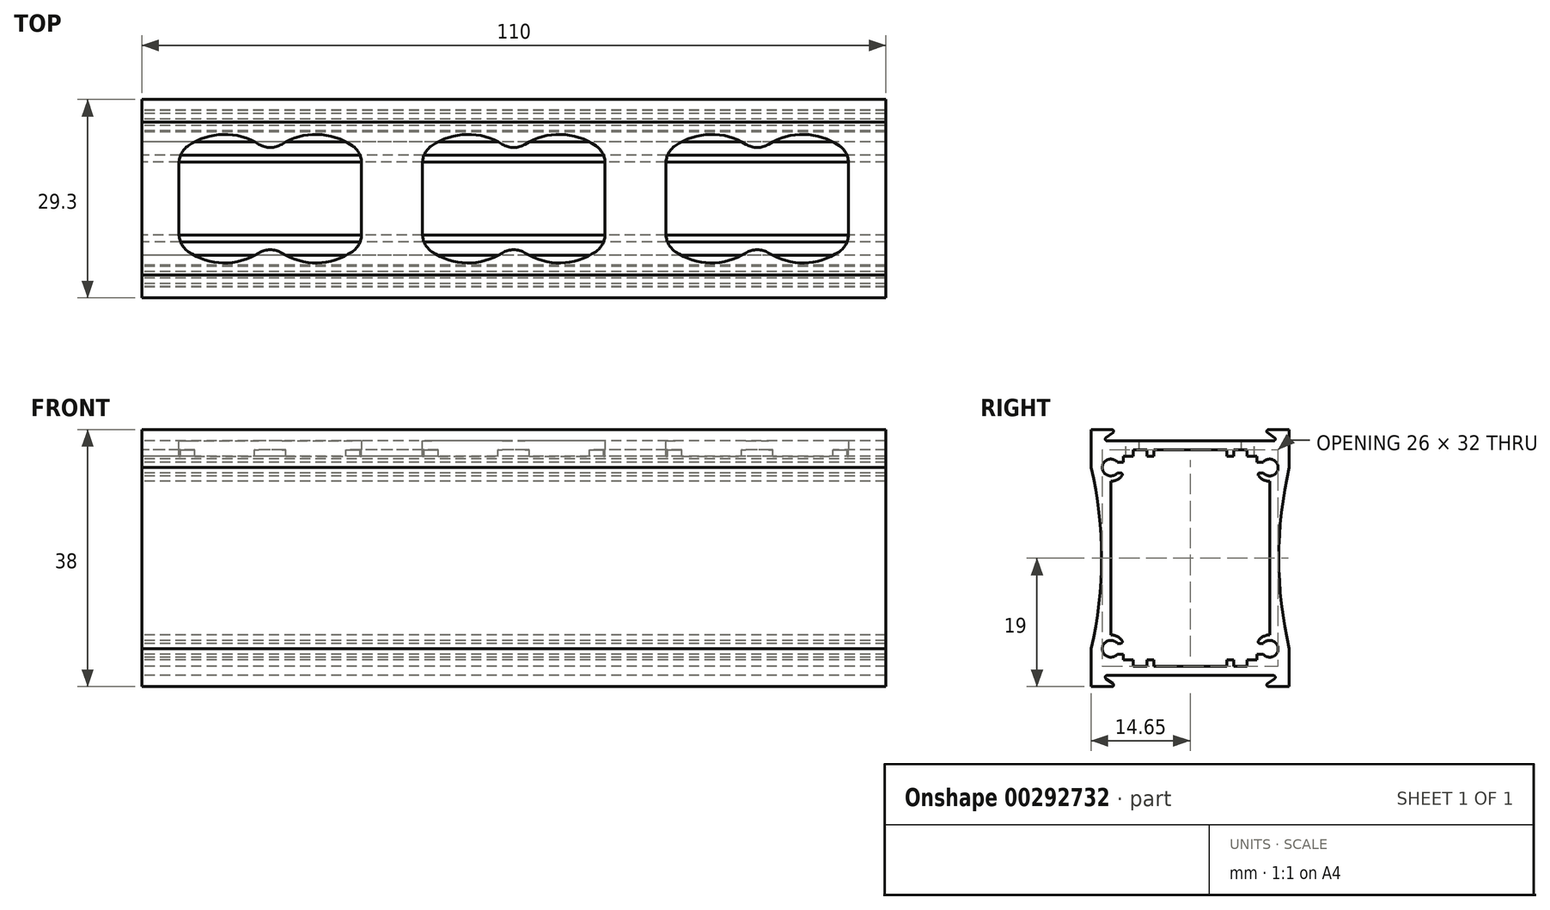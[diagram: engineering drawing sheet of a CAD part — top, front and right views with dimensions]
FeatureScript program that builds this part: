
annotation { "Feature Type Name" : "Feature", "Feature Type Description" : "" }
export const myFeature = defineFeature(function(context is Context, id is Id, definition is map)
    precondition{}
    {
        {
            var Q0;
            Q0=qCreatedBy(makeId("Right.planeOp"),FACE);
            var sketch = newSketch(context, id + "F0", { "sketchPlane" : qUnion([Q0])});
            skPoint(sketch, "E0.middle", {"position": v(0, 0) * mm});
            skLineSegment(sketch, "E1.0", {"start": v(0, 17.35) * mm, "end": v(-12.32, 17.35) * mm});
            skLineSegment(sketch, "E1.3", {"start": v(-13.1, 17.35) * mm, "end": v(-13.1, 0) * mm, "construction": true});
            skLineSegment(sketch, "E2.bottom", {"start": v(-11.57, 19) * mm, "end": v(-14.65, 19) * mm});
            skLineSegment(sketch, "E2.right", {"start": v(-14.65, 19) * mm, "end": v(-14.65, 13.4) * mm});
            skLineSegment(sketch, "E3", {"start": v(0, 0) * mm, "end": v(0, 16) * mm, "construction": true});
            skLineSegment(sketch, "E4", {"start": v(0, 0) * mm, "end": v(-11.75, 0) * mm, "construction": true});
            skArc(sketch, "E5", {"start": v(-10.79, 14.2) * mm, "mid": v(-13, 13.4) * mm, "end": v(-10.79, 12.6) * mm});
            skArc(sketch, "E6", {"start": v(-13.1, 0) * mm, "mid": v(-13.49, 6.74) * mm, "end": v(-14.65, 13.4) * mm});
            skLineSegment(sketch, "E7", {"start": v(-11.75, 13.4) * mm, "end": v(-14.65, 13.4) * mm, "construction": true});
            skArc(sketch, "E8.0", {"start": v(-11.75, 11.35) * mm, "mid": v(-10.81, 11.58) * mm, "end": v(-10.08, 12.2) * mm});
            skLineSegment(sketch, "E9.trimOffspring", {"start": v(-11.75, 11.35) * mm, "end": v(-11.75, 0) * mm});
            skLineSegment(sketch, "E10", {"start": v(-11.75, 13.4) * mm, "end": v(-9.7, 13.4) * mm, "construction": true});
            skLineSegment(sketch, "E11.0", {"start": v(-10.79, 12.6) * mm, "end": v(-10.29, 12.6) * mm});
            skLineSegment(sketch, "E12", {"start": v(-11.75, 16) * mm, "end": v(-11.75, 11.35) * mm, "construction": true});
            skLineSegment(sketch, "E13.trimOffspring", {"start": v(-10.79, 14.2) * mm, "end": v(-9.86, 14.2) * mm});
            skLineSegment(sketch, "E14", {"start": v(-10.79, 14.2) * mm, "end": v(-10.79, 12.6) * mm, "construction": true});
            skLineSegment(sketch, "E15", {"start": v(-9.86, 14.2) * mm, "end": v(-9.86, 15.05) * mm});
            skLineSegment(sketch, "E16", {"start": v(-9.86, 15.05) * mm, "end": v(-8.4, 15.05) * mm});
            skLineSegment(sketch, "E17", {"start": v(-8.4, 15.05) * mm, "end": v(-8.4, 16) * mm});
            skLineSegment(sketch, "E18", {"start": v(-8.4, 16) * mm, "end": v(-6.4, 16) * mm});
            skLineSegment(sketch, "E19", {"start": v(-6.4, 16) * mm, "end": v(-6.4, 15.05) * mm});
            skLineSegment(sketch, "E20", {"start": v(-6.4, 15.05) * mm, "end": v(-5.4, 15.05) * mm});
            skLineSegment(sketch, "E21", {"start": v(-5.4, 15.05) * mm, "end": v(-5.4, 16) * mm});
            skLineSegment(sketch, "E22", {"start": v(-5.4, 16) * mm, "end": v(0, 16) * mm});
            skLineSegment(sketch, "E23", {"start": v(-10.79, 14.2) * mm, "end": v(-10.79, 19) * mm, "construction": true});
            skLineSegment(sketch, "E24", {"start": v(-12.47, 17.8) * mm, "end": v(-11.42, 18.55) * mm});
            skPoint(sketch, "E25.visualSharp", {"position": v(-10.79, 19) * mm});
            skArc(sketch, "E25.filletArc", {"start": v(-11.42, 18.55) * mm, "mid": v(-11.33, 18.83) * mm, "end": v(-11.57, 19) * mm});
            skPoint(sketch, "E26.visualSharp", {"position": v(-13.1, 17.35) * mm});
            skArc(sketch, "E26.filletArc", {"start": v(-12.47, 17.8) * mm, "mid": v(-12.56, 17.52) * mm, "end": v(-12.32, 17.35) * mm});
            skPoint(sketch, "E27.visualSharp", {"position": v(-9.86, 12.6) * mm});
            skArc(sketch, "E27.filletArc", {"start": v(-10.08, 12.2) * mm, "mid": v(-10.07, 12.46) * mm, "end": v(-10.29, 12.6) * mm});
            skArc(sketch, "E28.MirrorCS", {"start": v(10.08, 12.2) * mm, "mid": v(10.07, 12.46) * mm, "end": v(10.29, 12.6) * mm});
            skLineSegment(sketch, "E29.MirrorCS", {"start": v(10.79, 12.6) * mm, "end": v(10.29, 12.6) * mm});
            skLineSegment(sketch, "E30.MirrorCS", {"start": v(11.75, 13.4) * mm, "end": v(9.7, 13.4) * mm, "construction": true});
            skLineSegment(sketch, "E31.MirrorCS", {"start": v(10.79, 14.2) * mm, "end": v(10.79, 12.6) * mm, "construction": true});
            skLineSegment(sketch, "E32.MirrorCS", {"start": v(9.86, 15.05) * mm, "end": v(8.4, 15.05) * mm});
            skLineSegment(sketch, "E33.MirrorCS", {"start": v(12.47, 17.8) * mm, "end": v(11.42, 18.55) * mm});
            skLineSegment(sketch, "E34.MirrorCS", {"start": v(10.79, 14.2) * mm, "end": v(9.86, 14.2) * mm});
            skLineSegment(sketch, "E35.MirrorCS", {"start": v(9.86, 14.2) * mm, "end": v(9.86, 15.05) * mm});
            skArc(sketch, "E36.MirrorCS", {"start": v(11.75, 11.35) * mm, "mid": v(10.81, 11.58) * mm, "end": v(10.08, 12.2) * mm});
            skArc(sketch, "E37.MirrorCS", {"start": v(12.47, 17.8) * mm, "mid": v(12.56, 17.52) * mm, "end": v(12.32, 17.35) * mm});
            skArc(sketch, "E38.MirrorCS", {"start": v(11.42, 18.55) * mm, "mid": v(11.33, 18.83) * mm, "end": v(11.57, 19) * mm});
            skLineSegment(sketch, "E39.MirrorCS", {"start": v(5.4, 15.05) * mm, "end": v(5.4, 16) * mm});
            skLineSegment(sketch, "E40.MirrorCS", {"start": v(6.4, 15.05) * mm, "end": v(5.4, 15.05) * mm});
            skLineSegment(sketch, "E41.MirrorCS", {"start": v(8.4, 15.05) * mm, "end": v(8.4, 16) * mm});
            skLineSegment(sketch, "E42.MirrorCS", {"start": v(8.4, 16) * mm, "end": v(6.4, 16) * mm});
            skLineSegment(sketch, "E43.MirrorCS", {"start": v(6.4, 16) * mm, "end": v(6.4, 15.05) * mm});
            skLineSegment(sketch, "E44.MirrorCS", {"start": v(11.75, 13.4) * mm, "end": v(14.65, 13.4) * mm, "construction": true});
            skLineSegment(sketch, "E45.MirrorCS", {"start": v(10.79, 14.2) * mm, "end": v(10.79, 19) * mm, "construction": true});
            skPoint(sketch, "E46.MirrorP", {"position": v(9.86, 12.6) * mm});
            skLineSegment(sketch, "E47.MirrorCS", {"start": v(11.75, 16) * mm, "end": v(11.75, 11.35) * mm, "construction": true});
            skLineSegment(sketch, "E48.MirrorCS", {"start": v(11.57, 19) * mm, "end": v(14.65, 19) * mm});
            skArc(sketch, "E49.MirrorCS", {"start": v(10.79, 14.2) * mm, "mid": v(13, 13.4) * mm, "end": v(10.79, 12.6) * mm});
            skLineSegment(sketch, "E50.MirrorCS", {"start": v(11.75, 11.35) * mm, "end": v(11.75, 0) * mm});
            skPoint(sketch, "E51.MirrorP", {"position": v(10.79, 19) * mm});
            skPoint(sketch, "E52.MirrorP", {"position": v(13.1, 17.35) * mm});
            skLineSegment(sketch, "E53.MirrorCS", {"start": v(0, 0) * mm, "end": v(11.75, 0) * mm, "construction": true});
            skArc(sketch, "E54.MirrorCS", {"start": v(13.1, 0) * mm, "mid": v(13.49, 6.74) * mm, "end": v(14.65, 13.4) * mm});
            skLineSegment(sketch, "E55.MirrorCS", {"start": v(5.4, 16) * mm, "end": v(0, 16) * mm});
            skLineSegment(sketch, "E56.MirrorCS", {"start": v(0, 17.35) * mm, "end": v(12.32, 17.35) * mm});
            skLineSegment(sketch, "E57.MirrorCS", {"start": v(13.1, 17.35) * mm, "end": v(13.1, 0) * mm, "construction": true});
            skLineSegment(sketch, "E58.MirrorCS", {"start": v(14.65, 19) * mm, "end": v(14.65, 13.4) * mm});
            skLineSegment(sketch, "E59.MirrorCS", {"start": v(-10.79, -12.6) * mm, "end": v(-10.29, -12.6) * mm});
            skArc(sketch, "E60.MirrorCS", {"start": v(-10.08, -12.2) * mm, "mid": v(-10.07, -12.46) * mm, "end": v(-10.29, -12.6) * mm});
            skLineSegment(sketch, "E61.MirrorCS", {"start": v(-11.75, -13.4) * mm, "end": v(-9.7, -13.4) * mm, "construction": true});
            skLineSegment(sketch, "E62.MirrorCS", {"start": v(11.75, -13.4) * mm, "end": v(9.7, -13.4) * mm, "construction": true});
            skLineSegment(sketch, "E63.MirrorCS", {"start": v(10.79, -12.6) * mm, "end": v(10.29, -12.6) * mm});
            skArc(sketch, "E64.MirrorCS", {"start": v(10.08, -12.2) * mm, "mid": v(10.07, -12.46) * mm, "end": v(10.29, -12.6) * mm});
            skLineSegment(sketch, "E65.MirrorCS", {"start": v(-10.79, -14.2) * mm, "end": v(-10.79, -12.6) * mm, "construction": true});
            skLineSegment(sketch, "E66.MirrorCS", {"start": v(-12.47, -17.8) * mm, "end": v(-11.42, -18.55) * mm});
            skLineSegment(sketch, "E67.MirrorCS", {"start": v(12.47, -17.8) * mm, "end": v(11.42, -18.55) * mm});
            skLineSegment(sketch, "E68.MirrorCS", {"start": v(-10.79, -14.2) * mm, "end": v(-9.86, -14.2) * mm});
            skArc(sketch, "E69.MirrorCS", {"start": v(12.47, -17.8) * mm, "mid": v(12.56, -17.52) * mm, "end": v(12.32, -17.35) * mm});
            skArc(sketch, "E70.MirrorCS", {"start": v(-12.47, -17.8) * mm, "mid": v(-12.56, -17.52) * mm, "end": v(-12.32, -17.35) * mm});
            skLineSegment(sketch, "E71.MirrorCS", {"start": v(10.79, -14.2) * mm, "end": v(10.79, -12.6) * mm, "construction": true});
            skArc(sketch, "E72.MirrorCS", {"start": v(11.42, -18.55) * mm, "mid": v(11.33, -18.83) * mm, "end": v(11.57, -19) * mm});
            skArc(sketch, "E73.MirrorCS", {"start": v(-11.42, -18.55) * mm, "mid": v(-11.33, -18.83) * mm, "end": v(-11.57, -19) * mm});
            skLineSegment(sketch, "E74.MirrorCS", {"start": v(9.86, -14.2) * mm, "end": v(9.86, -15.05) * mm});
            skArc(sketch, "E75.MirrorCS", {"start": v(-11.75, -11.35) * mm, "mid": v(-10.81, -11.58) * mm, "end": v(-10.08, -12.2) * mm});
            skLineSegment(sketch, "E76.MirrorCS", {"start": v(10.79, -14.2) * mm, "end": v(9.86, -14.2) * mm});
            skLineSegment(sketch, "E77.MirrorCS", {"start": v(-9.86, -14.2) * mm, "end": v(-9.86, -15.05) * mm});
            skLineSegment(sketch, "E78.MirrorCS", {"start": v(-8.4, -15.05) * mm, "end": v(-8.4, -16) * mm});
            skLineSegment(sketch, "E79.MirrorCS", {"start": v(-5.4, -15.05) * mm, "end": v(-5.4, -16) * mm});
            skLineSegment(sketch, "E80.MirrorCS", {"start": v(-6.4, -16) * mm, "end": v(-6.4, -15.05) * mm});
            skLineSegment(sketch, "E81.MirrorCS", {"start": v(-6.4, -15.05) * mm, "end": v(-5.4, -15.05) * mm});
            skLineSegment(sketch, "E82.MirrorCS", {"start": v(-9.86, -15.05) * mm, "end": v(-8.4, -15.05) * mm});
            skArc(sketch, "E83.MirrorCS", {"start": v(11.75, -11.35) * mm, "mid": v(10.81, -11.58) * mm, "end": v(10.08, -12.2) * mm});
            skLineSegment(sketch, "E84.MirrorCS", {"start": v(5.4, -15.05) * mm, "end": v(5.4, -16) * mm});
            skLineSegment(sketch, "E85.MirrorCS", {"start": v(-8.4, -16) * mm, "end": v(-6.4, -16) * mm});
            skLineSegment(sketch, "E86.MirrorCS", {"start": v(8.4, -15.05) * mm, "end": v(8.4, -16) * mm});
            skLineSegment(sketch, "E87.MirrorCS", {"start": v(6.4, -15.05) * mm, "end": v(5.4, -15.05) * mm});
            skLineSegment(sketch, "E88.MirrorCS", {"start": v(6.4, -16) * mm, "end": v(6.4, -15.05) * mm});
            skLineSegment(sketch, "E89.MirrorCS", {"start": v(8.4, -16) * mm, "end": v(6.4, -16) * mm});
            skLineSegment(sketch, "E90.MirrorCS", {"start": v(9.86, -15.05) * mm, "end": v(8.4, -15.05) * mm});
            skLineSegment(sketch, "E91.MirrorCS", {"start": v(11.75, -16) * mm, "end": v(11.75, -11.35) * mm, "construction": true});
            skPoint(sketch, "E92.MirrorP", {"position": v(-9.86, -12.6) * mm});
            skLineSegment(sketch, "E93.MirrorCS", {"start": v(-10.79, -14.2) * mm, "end": v(-10.79, -19) * mm, "construction": true});
            skLineSegment(sketch, "E94.MirrorCS", {"start": v(-11.75, -16) * mm, "end": v(-11.75, -11.35) * mm, "construction": true});
            skLineSegment(sketch, "E95.MirrorCS", {"start": v(-11.57, -19) * mm, "end": v(-14.65, -19) * mm});
            skLineSegment(sketch, "E96.MirrorCS", {"start": v(-11.75, -13.4) * mm, "end": v(-14.65, -13.4) * mm, "construction": true});
            skPoint(sketch, "E97.MirrorP", {"position": v(-10.79, -19) * mm});
            skLineSegment(sketch, "E98.MirrorCS", {"start": v(14.65, -19) * mm, "end": v(14.65, -13.4) * mm});
            skLineSegment(sketch, "E99.MirrorCS", {"start": v(-13.1, -17.35) * mm, "end": v(-13.1, 0) * mm, "construction": true});
            skPoint(sketch, "E100.MirrorP", {"position": v(-13.1, -17.35) * mm});
            skLineSegment(sketch, "E101.MirrorCS", {"start": v(-11.75, -11.35) * mm, "end": v(-11.75, 0) * mm});
            skPoint(sketch, "E102.MirrorP", {"position": v(10.79, -19) * mm});
            skLineSegment(sketch, "E103.MirrorCS", {"start": v(5.4, -16) * mm, "end": v(0, -16) * mm});
            skLineSegment(sketch, "E104.MirrorCS", {"start": v(11.75, -11.35) * mm, "end": v(11.75, 0) * mm});
            skLineSegment(sketch, "E105.MirrorCS", {"start": v(10.79, -14.2) * mm, "end": v(10.79, -19) * mm, "construction": true});
            skPoint(sketch, "E106.MirrorP", {"position": v(9.86, -12.6) * mm});
            skLineSegment(sketch, "E107.MirrorCS", {"start": v(0, -17.35) * mm, "end": v(12.32, -17.35) * mm});
            skLineSegment(sketch, "E108.MirrorCS", {"start": v(-5.4, -16) * mm, "end": v(0, -16) * mm});
            skLineSegment(sketch, "E109.MirrorCS", {"start": v(13.1, -17.35) * mm, "end": v(13.1, 0) * mm, "construction": true});
            skArc(sketch, "E110.MirrorCS", {"start": v(10.79, -14.2) * mm, "mid": v(13, -13.4) * mm, "end": v(10.79, -12.6) * mm});
            skPoint(sketch, "E111.MirrorP", {"position": v(13.1, -17.35) * mm});
            skArc(sketch, "E112.MirrorCS", {"start": v(-10.79, -14.2) * mm, "mid": v(-13, -13.4) * mm, "end": v(-10.79, -12.6) * mm});
            skLineSegment(sketch, "E113.MirrorCS", {"start": v(11.57, -19) * mm, "end": v(14.65, -19) * mm});
            skLineSegment(sketch, "E114.MirrorCS", {"start": v(0, 0) * mm, "end": v(0, -16) * mm, "construction": true});
            skLineSegment(sketch, "E115.MirrorCS", {"start": v(-14.65, -19) * mm, "end": v(-14.65, -13.4) * mm});
            skLineSegment(sketch, "E116.MirrorCS", {"start": v(0, -17.35) * mm, "end": v(-12.32, -17.35) * mm});
            skLineSegment(sketch, "E117.MirrorCS", {"start": v(11.75, -13.4) * mm, "end": v(14.65, -13.4) * mm, "construction": true});
            skArc(sketch, "E118.MirrorCS", {"start": v(-13.1, 0) * mm, "mid": v(-13.49, -6.74) * mm, "end": v(-14.65, -13.4) * mm});
            skArc(sketch, "E119.MirrorCS", {"start": v(13.1, 0) * mm, "mid": v(13.49, -6.74) * mm, "end": v(14.65, -13.4) * mm});
            skSolve(sketch);
        }
        {
            var Q0;
            Q0=makeQuery(id+"F0.imprint","IMPRINT",FACE,{"disambiguationData":[TD([[makeQuery(id+"F0.imprint","IMPRINT",EDGE,{"derivedFrom":sQuery(id+"F0.wireOp",EDGE,"E1.0")}),1.0]])]});
            extrude(context, id + "F1", {"entities" : qUnion([Q0]), "depth" : 110 * mm});
        }
        {
            var Q0;
            Q0=makeQuery(id+"F1.opExtrude","SWEPT_FACE",FACE,{"disambiguationData":[OSD([sQuery(id+"F0.wireOp",EDGE,"E48.MirrorCS")])]});
            var sketch = newSketch(context, id + "F2", { "sketchPlane" : qUnion([Q0])});
            skLineSegment(sketch, "E120", {"start": v(0, 0) * mm, "end": v(110, 0) * mm, "construction": true});
            skLineSegment(sketch, "E121.left", {"start": v(19, -6.68) * mm, "end": v(19, 6.68) * mm});
            skLineSegment(sketch, "E121.right", {"start": v(5.5, -6.68) * mm, "end": v(5.5, 6.68) * mm});
            skPoint(sketch, "E121.middle", {"position": v(12.25, 0) * mm});
            skArc(sketch, "E122", {"start": v(19, 6.68) * mm, "mid": v(12.25, 9.5) * mm, "end": v(5.5, 6.68) * mm});
            skArc(sketch, "E123.trimOffspring", {"start": v(5.5, -6.68) * mm, "mid": v(12.25, -9.5) * mm, "end": v(19, -6.68) * mm});
            skArc(sketch, "E124.1.0.0", {"start": v(32.5, 6.68) * mm, "mid": v(25.75, 9.5) * mm, "end": v(19, 6.68) * mm});
            skLineSegment(sketch, "E124.1.0.1", {"start": v(32.5, -6.68) * mm, "end": v(32.5, 6.68) * mm});
            skArc(sketch, "E124.1.0.2", {"start": v(19, -6.68) * mm, "mid": v(25.75, -9.5) * mm, "end": v(32.5, -6.68) * mm});
            skLineSegment(sketch, "E124.direction1", {"start": v(12.25, 0) * mm, "end": v(25.75, 0) * mm, "construction": true});
            skArc(sketch, "E125.1.0.0", {"start": v(55, 6.68) * mm, "mid": v(48.25, 9.5) * mm, "end": v(41.5, 6.68) * mm});
            skLineSegment(sketch, "E125.1.0.1", {"start": v(55, -6.68) * mm, "end": v(55, 6.68) * mm});
            skArc(sketch, "E125.1.0.2", {"start": v(68.5, 6.68) * mm, "mid": v(61.75, 9.5) * mm, "end": v(55, 6.68) * mm});
            skLineSegment(sketch, "E125.1.0.3", {"start": v(55, -6.68) * mm, "end": v(55, 6.68) * mm});
            skLineSegment(sketch, "E125.1.0.4", {"start": v(68.5, -6.68) * mm, "end": v(68.5, 6.68) * mm});
            skArc(sketch, "E125.1.0.5", {"start": v(55, -6.68) * mm, "mid": v(61.75, -9.5) * mm, "end": v(68.5, -6.68) * mm});
            skArc(sketch, "E125.1.0.6", {"start": v(41.5, -6.68) * mm, "mid": v(48.25, -9.5) * mm, "end": v(55, -6.68) * mm});
            skLineSegment(sketch, "E125.1.0.7", {"start": v(41.5, -6.68) * mm, "end": v(41.5, 6.68) * mm});
            skArc(sketch, "E125.2.0.0", {"start": v(91, 6.68) * mm, "mid": v(84.25, 9.5) * mm, "end": v(77.5, 6.68) * mm});
            skLineSegment(sketch, "E125.2.0.1", {"start": v(91, -6.68) * mm, "end": v(91, 6.68) * mm});
            skArc(sketch, "E125.2.0.2", {"start": v(104.5, 6.68) * mm, "mid": v(97.75, 9.5) * mm, "end": v(91, 6.68) * mm});
            skLineSegment(sketch, "E125.2.0.3", {"start": v(91, -6.68) * mm, "end": v(91, 6.68) * mm});
            skLineSegment(sketch, "E125.2.0.4", {"start": v(104.5, -6.68) * mm, "end": v(104.5, 6.68) * mm});
            skArc(sketch, "E125.2.0.5", {"start": v(91, -6.68) * mm, "mid": v(97.75, -9.5) * mm, "end": v(104.5, -6.68) * mm});
            skArc(sketch, "E125.2.0.6", {"start": v(77.5, -6.68) * mm, "mid": v(84.25, -9.5) * mm, "end": v(91, -6.68) * mm});
            skLineSegment(sketch, "E125.2.0.7", {"start": v(77.5, -6.68) * mm, "end": v(77.5, 6.68) * mm});
            skLineSegment(sketch, "E125.direction1", {"start": v(12.25, 0) * mm, "end": v(48.25, 0) * mm, "construction": true});
            skPoint(sketch, "E126", {"position": v(77.5, 0) * mm});
            skLineSegment(sketch, "E127", {"start": v(55, 6.68) * mm, "end": v(55, -6.68) * mm, "construction": true});
            skPoint(sketch, "E128", {"position": v(55, 0) * mm});
            skLineSegment(sketch, "E129", {"start": v(37, 4) * mm, "end": v(37, -4) * mm, "construction": true});
            skLineSegment(sketch, "E130", {"start": v(73, 4) * mm, "end": v(73, -4) * mm, "construction": true});
            skLineSegment(sketch, "E131", {"start": v(37, 4) * mm, "end": v(73, -4) * mm, "construction": true});
            skCircle(sketch, "E132", {"center": v(37, 4) * mm, "radius": 1.5 * mm, "construction": true});
            skCircle(sketch, "E133", {"center": v(37, -4) * mm, "radius": 1.5 * mm, "construction": true});
            skCircle(sketch, "E134", {"center": v(73, -4) * mm, "radius": 1.5 * mm, "construction": true});
            skCircle(sketch, "E135", {"center": v(73, 4) * mm, "radius": 1.5 * mm, "construction": true});
            skSolve(sketch);
        }
        {
            var Q0;
            Q0 = qSketchRegion(id + "F2", true);
            extrude(context, id + "F3", {"entities" : qUnion([Q0]), "operationType" : NewBodyOperationType.REMOVE, "oppositeDirection" : true, "depth" : 8 * mm});
        }
        {
            var Q0;
            Q0=makeQuery(id+"F3.boolean.opBoolean","COPY",EDGE,{"derivedFrom":makeQuery(id+"F3.opExtrude","SWEPT_EDGE",EDGE,{"disambiguationData":[OSD([sQuery(id+"F2.wireOp",EDGE,"E124.1.0.1"),sQuery(id+"F2.wireOp",EDGE,"E124.1.0.2")])]})});
            var Q1;
            Q1=makeQuery(id+"F3.boolean.opBoolean","COPY",EDGE,{"derivedFrom":makeQuery(id+"F3.opExtrude","SWEPT_EDGE",EDGE,{"disambiguationData":[OSD([sQuery(id+"F2.wireOp",EDGE,"E124.1.0.0"),sQuery(id+"F2.wireOp",EDGE,"E124.1.0.1")])]})});
            var Q2;
            Q2=makeQuery(id+"F3.boolean.opBoolean","COPY",EDGE,{"derivedFrom":makeQuery(id+"F3.opExtrude","SWEPT_EDGE",EDGE,{"disambiguationData":[OSD([sQuery(id+"F2.wireOp",EDGE,"E121.left"),sQuery(id+"F2.wireOp",EDGE,"E122")])]})});
            var Q3;
            Q3=makeQuery(id+"F3.boolean.opBoolean","COPY",EDGE,{"derivedFrom":makeQuery(id+"F3.opExtrude","SWEPT_EDGE",EDGE,{"disambiguationData":[OSD([sQuery(id+"F2.wireOp",EDGE,"E121.left"),sQuery(id+"F2.wireOp",EDGE,"E123.trimOffspring")])]})});
            var Q4;
            Q4=makeQuery(id+"F3.boolean.opBoolean","COPY",EDGE,{"derivedFrom":makeQuery(id+"F3.opExtrude","SWEPT_EDGE",EDGE,{"disambiguationData":[OSD([sQuery(id+"F2.wireOp",EDGE,"E125.1.0.1"),sQuery(id+"F2.wireOp",EDGE,"E125.1.0.6")])]})});
            var Q5;
            Q5=makeQuery(id+"F3.boolean.opBoolean","COPY",EDGE,{"derivedFrom":makeQuery(id+"F3.opExtrude","SWEPT_EDGE",EDGE,{"disambiguationData":[OSD([sQuery(id+"F2.wireOp",EDGE,"E125.1.0.0"),sQuery(id+"F2.wireOp",EDGE,"E125.1.0.1")])]})});
            var Q6;
            Q6=makeQuery(id+"F3.boolean.opBoolean","COPY",EDGE,{"derivedFrom":makeQuery(id+"F3.opExtrude","SWEPT_EDGE",EDGE,{"disambiguationData":[OSD([sQuery(id+"F2.wireOp",EDGE,"E125.1.0.2"),sQuery(id+"F2.wireOp",EDGE,"E125.1.0.4")])]})});
            var Q7;
            Q7=makeQuery(id+"F3.boolean.opBoolean","COPY",EDGE,{"derivedFrom":makeQuery(id+"F3.opExtrude","SWEPT_EDGE",EDGE,{"disambiguationData":[OSD([sQuery(id+"F2.wireOp",EDGE,"E125.1.0.4"),sQuery(id+"F2.wireOp",EDGE,"E125.1.0.5")])]})});
            var Q8;
            Q8=makeQuery(id+"F3.boolean.opBoolean","COPY",EDGE,{"derivedFrom":makeQuery(id+"F3.opExtrude","SWEPT_EDGE",EDGE,{"disambiguationData":[OSD([sQuery(id+"F2.wireOp",EDGE,"E125.2.0.1"),sQuery(id+"F2.wireOp",EDGE,"E125.2.0.6")])]})});
            var Q9;
            Q9=makeQuery(id+"F3.boolean.opBoolean","COPY",EDGE,{"derivedFrom":makeQuery(id+"F3.opExtrude","SWEPT_EDGE",EDGE,{"disambiguationData":[OSD([sQuery(id+"F2.wireOp",EDGE,"E125.2.0.0"),sQuery(id+"F2.wireOp",EDGE,"E125.2.0.1")])]})});
            var Q10;
            Q10=makeQuery(id+"F3.boolean.opBoolean","COPY",EDGE,{"derivedFrom":makeQuery(id+"F3.opExtrude","SWEPT_EDGE",EDGE,{"disambiguationData":[OSD([sQuery(id+"F2.wireOp",EDGE,"E125.2.0.2"),sQuery(id+"F2.wireOp",EDGE,"E125.2.0.4")])]})});
            var Q11;
            Q11=makeQuery(id+"F3.boolean.opBoolean","COPY",EDGE,{"derivedFrom":makeQuery(id+"F3.opExtrude","SWEPT_EDGE",EDGE,{"disambiguationData":[OSD([sQuery(id+"F2.wireOp",EDGE,"E125.2.0.4"),sQuery(id+"F2.wireOp",EDGE,"E125.2.0.5")])]})});
            var Q12;
            Q12=makeQuery(id+"F3.boolean.opBoolean","COPY",EDGE,{"derivedFrom":makeQuery(id+"F3.opExtrude","SWEPT_EDGE",EDGE,{"disambiguationData":[OSD([sQuery(id+"F2.wireOp",EDGE,"E125.2.0.2"),sQuery(id+"F2.wireOp",EDGE,"E125.2.0.3")])]})});
            var Q13;
            Q13=makeQuery(id+"F3.boolean.opBoolean","COPY",EDGE,{"derivedFrom":makeQuery(id+"F3.opExtrude","SWEPT_EDGE",EDGE,{"disambiguationData":[OSD([sQuery(id+"F2.wireOp",EDGE,"E125.2.0.3"),sQuery(id+"F2.wireOp",EDGE,"E125.2.0.5")])]})});
            var Q14;
            Q14=makeQuery(id+"F3.boolean.opBoolean","COPY",EDGE,{"derivedFrom":makeQuery(id+"F3.opExtrude","SWEPT_EDGE",EDGE,{"disambiguationData":[OSD([sQuery(id+"F2.wireOp",EDGE,"E125.2.0.6"),sQuery(id+"F2.wireOp",EDGE,"E125.2.0.7")])]})});
            var Q15;
            Q15=makeQuery(id+"F3.boolean.opBoolean","COPY",EDGE,{"derivedFrom":makeQuery(id+"F3.opExtrude","SWEPT_EDGE",EDGE,{"disambiguationData":[OSD([sQuery(id+"F2.wireOp",EDGE,"E125.2.0.0"),sQuery(id+"F2.wireOp",EDGE,"E125.2.0.7")])]})});
            var Q16;
            Q16=makeQuery(id+"F3.boolean.opBoolean","COPY",EDGE,{"derivedFrom":makeQuery(id+"F3.opExtrude","SWEPT_EDGE",EDGE,{"disambiguationData":[OSD([sQuery(id+"F2.wireOp",EDGE,"E125.1.0.2"),sQuery(id+"F2.wireOp",EDGE,"E125.1.0.3")])]})});
            var Q17;
            Q17=makeQuery(id+"F3.boolean.opBoolean","COPY",EDGE,{"derivedFrom":makeQuery(id+"F3.opExtrude","SWEPT_EDGE",EDGE,{"disambiguationData":[OSD([sQuery(id+"F2.wireOp",EDGE,"E125.1.0.3"),sQuery(id+"F2.wireOp",EDGE,"E125.1.0.5")])]})});
            var Q18;
            Q18=makeQuery(id+"F3.boolean.opBoolean","COPY",EDGE,{"derivedFrom":makeQuery(id+"F3.opExtrude","SWEPT_EDGE",EDGE,{"disambiguationData":[OSD([sQuery(id+"F2.wireOp",EDGE,"E125.1.0.6"),sQuery(id+"F2.wireOp",EDGE,"E125.1.0.7")])]})});
            var Q19;
            Q19=makeQuery(id+"F3.boolean.opBoolean","COPY",EDGE,{"derivedFrom":makeQuery(id+"F3.opExtrude","SWEPT_EDGE",EDGE,{"disambiguationData":[OSD([sQuery(id+"F2.wireOp",EDGE,"E125.1.0.0"),sQuery(id+"F2.wireOp",EDGE,"E125.1.0.7")])]})});
            var Q20;
            Q20=makeQuery(id+"F3.boolean.opBoolean","COPY",EDGE,{"derivedFrom":makeQuery(id+"F3.opExtrude","SWEPT_EDGE",EDGE,{"disambiguationData":[OSD([sQuery(id+"F2.wireOp",EDGE,"E124.1.0.0"),sQuery(id+"F2.wireOp",EDGE,"E121.left")])]})});
            var Q21;
            Q21=makeQuery(id+"F3.boolean.opBoolean","COPY",EDGE,{"derivedFrom":makeQuery(id+"F3.opExtrude","SWEPT_EDGE",EDGE,{"disambiguationData":[OSD([sQuery(id+"F2.wireOp",EDGE,"E124.1.0.2"),sQuery(id+"F2.wireOp",EDGE,"E121.left")])]})});
            var Q22;
            Q22=makeQuery(id+"F3.boolean.opBoolean","COPY",EDGE,{"derivedFrom":makeQuery(id+"F3.opExtrude","SWEPT_EDGE",EDGE,{"disambiguationData":[OSD([sQuery(id+"F2.wireOp",EDGE,"E121.right"),sQuery(id+"F2.wireOp",EDGE,"E123.trimOffspring")])]})});
            var Q23;
            Q23=makeQuery(id+"F3.boolean.opBoolean","COPY",EDGE,{"derivedFrom":makeQuery(id+"F3.opExtrude","SWEPT_EDGE",EDGE,{"disambiguationData":[OSD([sQuery(id+"F2.wireOp",EDGE,"E121.right"),sQuery(id+"F2.wireOp",EDGE,"E122")])]})});
            fillet(context, id + "F4", {"entities" : qUnion([Q0, Q1, Q2, Q3, Q4, Q5, Q6, Q7, Q8, Q9, Q10, Q11, Q12, Q13, Q14, Q15, Q16, Q17, Q18, Q19, Q20, Q21, Q22, Q23]), "radius" : 3.17 * mm, "tangentPropagation" : true, "allowEdgeOverflow" : false});
        }
    });
